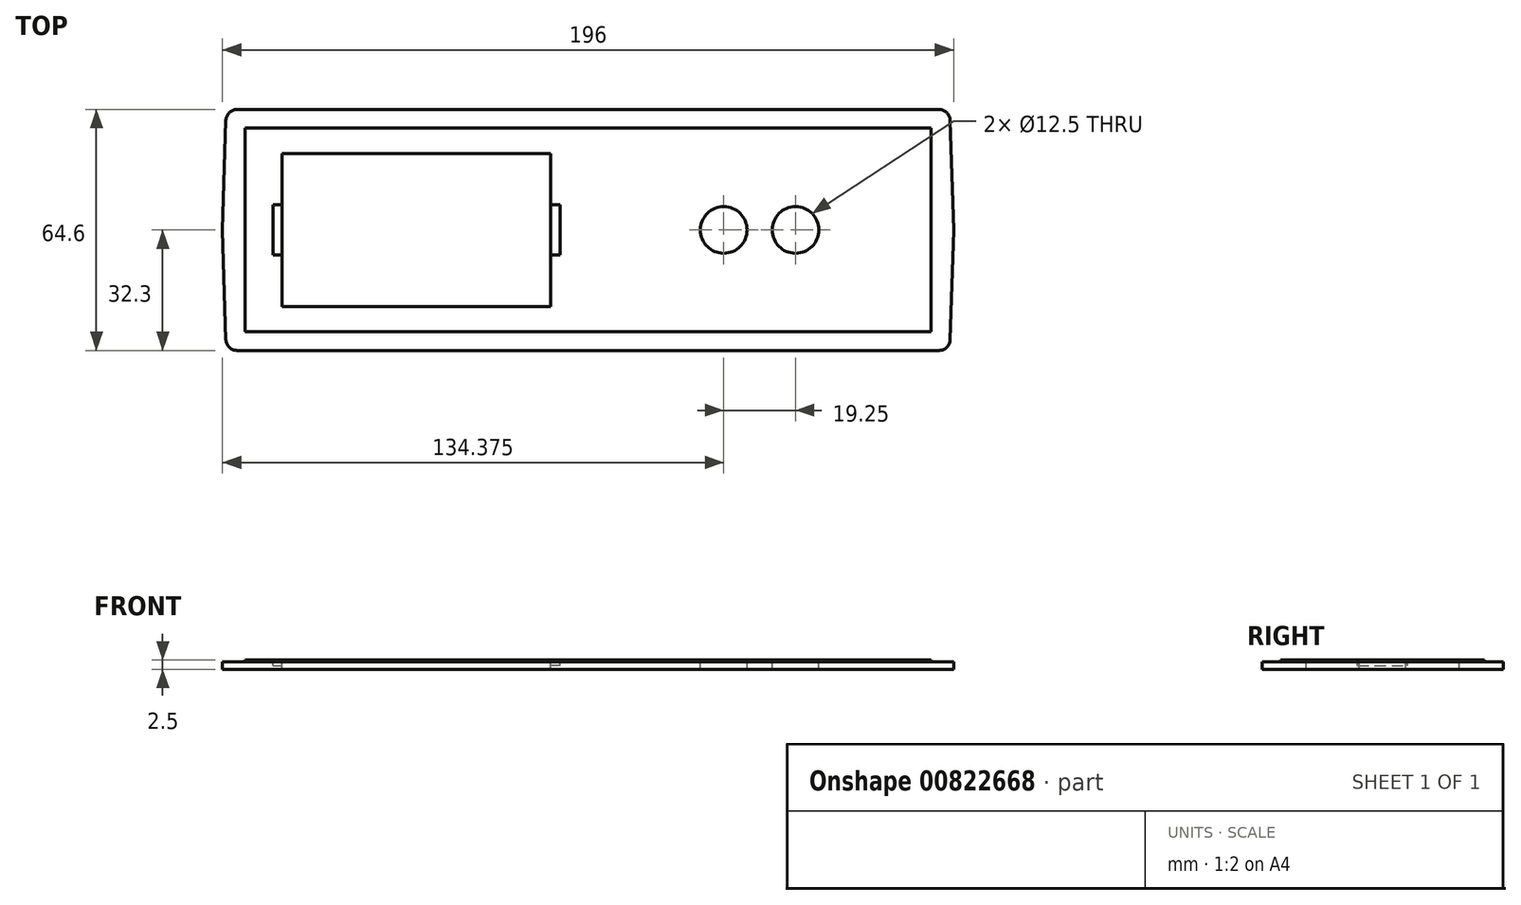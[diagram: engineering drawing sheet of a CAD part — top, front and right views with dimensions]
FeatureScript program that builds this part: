
annotation { "Feature Type Name" : "Feature", "Feature Type Description" : "" }
export const myFeature = defineFeature(function(context is Context, id is Id, definition is map)
    precondition{}
    {
        {
            var Q0;
            Q0=qCreatedBy(makeId("Top.planeOp"),FACE);
            var sketch = newSketch(context, id + "F0", { "sketchPlane" : qUnion([Q0])});
            skLineSegment(sketch, "E0.bottom", {"start": v(97, 32.3) * mm, "end": v(-97, 32.3) * mm});
            skLineSegment(sketch, "E0.top", {"start": v(97, -32.3) * mm, "end": v(-97, -32.3) * mm});
            skLineSegment(sketch, "E0.left", {"start": v(97, 32.3) * mm, "end": v(97, -32.3) * mm});
            skLineSegment(sketch, "E0.right", {"start": v(-97, 32.3) * mm, "end": v(-97, -32.3) * mm});
            skPoint(sketch, "E0.middle", {"position": v(0, 0) * mm});
            skLineSegment(sketch, "E1", {"start": v(98, 0) * mm, "end": v(97, -32.3) * mm});
            skPoint(sketch, "E1.startSnap0", {"position": v(97, 0) * mm});
            skLineSegment(sketch, "E2", {"start": v(98, 0) * mm, "end": v(97, 32.3) * mm});
            skLineSegment(sketch, "E3", {"start": v(-98, 0) * mm, "end": v(-97, 32.3) * mm});
            skLineSegment(sketch, "E4", {"start": v(-98, 0) * mm, "end": v(-97, -32.3) * mm});
            skSolve(sketch);
        }
        {
            var Q0;
            Q0=makeQuery(id+"F0.imprint","IMPRINT",FACE,{"disambiguationData":[TD([[makeQuery(id+"F0.imprint","IMPRINT",EDGE,{"derivedFrom":sQuery(id+"F0.wireOp",EDGE,"E0.bottom")}),1.0]])]});
            var Q1;
            Q1=makeQuery(id+"F0.imprint","IMPRINT",FACE,{"disambiguationData":[TD([[makeQuery(id+"F0.imprint","IMPRINT",EDGE,{"derivedFrom":sQuery(id+"F0.wireOp",EDGE,"E0.left")}),1.0]])]});
            var Q2;
            Q2=makeQuery(id+"F0.imprint","IMPRINT",FACE,{"disambiguationData":[TD([[makeQuery(id+"F0.imprint","IMPRINT",EDGE,{"derivedFrom":sQuery(id+"F0.wireOp",EDGE,"E0.right")}),-1.0]])]});
            extrude(context, id + "F1", {"entities" : qUnion([Q0, Q1, Q2]), "depth" : 2 * mm, "offsetDistance" : 25 * mm});
        }
        {
            var Q0;
            Q0=makeQuery(id+"F1.opExtrude","CAP_FACE",FACE,{"disambiguationData":[OSD([sQuery(id+"F0.wireOp",EDGE,"E0.bottom"),sQuery(id+"F0.wireOp",EDGE,"E0.top"),sQuery(id+"F0.wireOp",EDGE,"E0.left"),sQuery(id+"F0.wireOp",EDGE,"E0.right")])],"isStart":false});
            var sketch = newSketch(context, id + "F2", { "sketchPlane" : qUnion([Q0])});
            skLineSegment(sketch, "E5.bottom", {"start": v(92, 27.3) * mm, "end": v(-92, 27.3) * mm});
            skLineSegment(sketch, "E5.top", {"start": v(92, -27.3) * mm, "end": v(-92, -27.3) * mm});
            skLineSegment(sketch, "E5.left", {"start": v(92, 27.3) * mm, "end": v(92, -27.3) * mm});
            skLineSegment(sketch, "E5.right", {"start": v(-92, 27.3) * mm, "end": v(-92, -27.3) * mm});
            skPoint(sketch, "E5.middle", {"position": v(0, 0) * mm});
            skSolve(sketch);
        }
        {
            var Q0;
            Q0=makeQuery(id+"F2.imprint","IMPRINT",FACE,{"disambiguationData":[TD([[makeQuery(id+"F2.imprint","IMPRINT",EDGE,{"derivedFrom":sQuery(id+"F2.wireOp",EDGE,"E5.bottom")}),1.0]])]});
            extrude(context, id + "F3", {"entities" : qUnion([Q0]), "operationType" : NewBodyOperationType.ADD, "depth" : .5 * mm, "offsetDistance" : 25 * mm});
        }
        {
            var Q0;
            Q0=makeQuery(id+"F3.opExtrude","CAP_FACE",FACE,{"disambiguationData":[OSD([sQuery(id+"F2.wireOp",EDGE,"E5.bottom"),sQuery(id+"F2.wireOp",EDGE,"E5.top"),sQuery(id+"F2.wireOp",EDGE,"E5.left"),sQuery(id+"F2.wireOp",EDGE,"E5.right")])],"isStart":false});
            var sketch = newSketch(context, id + "F4", { "sketchPlane" : qUnion([Q0])});
            skLineSegment(sketch, "E6.bottom", {"start": v(-82, 20.5) * mm, "end": v(-10, 20.5) * mm});
            skLineSegment(sketch, "E6.top", {"start": v(-82, -20.5) * mm, "end": v(-10, -20.5) * mm});
            skLineSegment(sketch, "E6.left", {"start": v(-82, 20.5) * mm, "end": v(-82, -20.5) * mm});
            skLineSegment(sketch, "E6.right", {"start": v(-10, 20.5) * mm, "end": v(-10, -20.5) * mm});
            skLineSegment(sketch, "E7", {"start": v(-82, 20.5) * mm, "end": v(-82, 27.3) * mm, "construction": true});
            skLineSegment(sketch, "E8", {"start": v(-82, -20.5) * mm, "end": v(-82, -27.3) * mm, "construction": true});
            skLineSegment(sketch, "E9", {"start": v(-82, 20.5) * mm, "end": v(-92, 20.5) * mm, "construction": true});
            skLineSegment(sketch, "E10", {"start": v(-10, 20.5) * mm, "end": v(0, 20.5) * mm, "construction": true});
            skLineSegment(sketch, "E11.bottom", {"start": v(-84.5, 6.75) * mm, "end": v(-79.5, 6.75) * mm});
            skLineSegment(sketch, "E11.top", {"start": v(-84.5, -6.75) * mm, "end": v(-79.5, -6.75) * mm});
            skLineSegment(sketch, "E11.left", {"start": v(-84.5, 6.75) * mm, "end": v(-84.5, -6.75) * mm});
            skLineSegment(sketch, "E11.right", {"start": v(-79.5, 6.75) * mm, "end": v(-79.5, -6.75) * mm});
            skPoint(sketch, "E11.middle", {"position": v(-82, 0) * mm});
            skLineSegment(sketch, "E12.bottom", {"start": v(-7.5, 6.75) * mm, "end": v(-12.5, 6.75) * mm});
            skLineSegment(sketch, "E12.top", {"start": v(-7.5, -6.75) * mm, "end": v(-12.5, -6.75) * mm});
            skLineSegment(sketch, "E12.left", {"start": v(-7.5, 6.75) * mm, "end": v(-7.5, -6.75) * mm});
            skLineSegment(sketch, "E12.right", {"start": v(-12.5, 6.75) * mm, "end": v(-12.5, -6.75) * mm});
            skPoint(sketch, "E12.middle", {"position": v(-10, 0) * mm});
            skPoint(sketch, "E12.cornerSnap0", {"position": v(-82, 6.75) * mm});
            skCircle(sketch, "E13", {"center": v(36.37, 0) * mm, "radius": 6.25 * mm});
            skCircle(sketch, "E14", {"center": v(55.62, 0) * mm, "radius": 6.25 * mm});
            skLineSegment(sketch, "E15", {"start": v(36.37, 0) * mm, "end": v(0, 0) * mm, "construction": true});
            skLineSegment(sketch, "E16", {"start": v(55.62, 0) * mm, "end": v(92, 0) * mm, "construction": true});
            skSolve(sketch);
        }
        {
            var Q0;
            {var subQ8=sQuery(id+"F4.wireOp",EDGE,"E6.bottom");Q0=makeQuery(id+"F4.imprint","IMPRINT",FACE,{"disambiguationData":[TD([[makeQuery(id+"F4.imprint","IMPRINT",EDGE,{"derivedFrom":subQ8}),-1.0]])]});}
            var Q1;
            Q1=makeQuery(id+"F4.imprint","IMPRINT",FACE,{"disambiguationData":[TD([[makeQuery(id+"F4.imprint","IMPRINT",EDGE,{"derivedFrom":sQuery(id+"F4.wireOp",EDGE,"E13")}),1.0]])]});
            var Q2;
            Q2=makeQuery(id+"F4.imprint","IMPRINT",FACE,{"disambiguationData":[TD([[makeQuery(id+"F4.imprint","IMPRINT",EDGE,{"derivedFrom":sQuery(id+"F4.wireOp",EDGE,"E14")}),1.0]])]});
            var Q3;
            {var subQ5=sQuery(id+"F4.wireOp",EDGE,"E12.right");Q3=makeQuery(id+"F4.imprint","IMPRINT",FACE,{"disambiguationData":[TD([[makeQuery(id+"F4.imprint","IMPRINT",EDGE,{"derivedFrom":subQ5}),1.0]])]});}
            var Q4;
            {var subQ5=sQuery(id+"F4.wireOp",EDGE,"E11.right");Q4=makeQuery(id+"F4.imprint","IMPRINT",FACE,{"disambiguationData":[TD([[makeQuery(id+"F4.imprint","IMPRINT",EDGE,{"derivedFrom":subQ5}),-1.0]])]});}
            extrude(context, id + "F5", {"entities" : qUnion([Q0, Q1, Q2, Q3, Q4]), "operationType" : NewBodyOperationType.REMOVE, "oppositeDirection" : true, "depth" : 25 * mm, "offsetDistance" : 25 * mm});
        }
        {
            var Q0;
            Q0=makeQuery(id+"F1.opExtrude","SWEPT_EDGE",EDGE,{"disambiguationData":[OSD([sQuery(id+"F0.wireOp",EDGE,"E0.top"),sQuery(id+"F0.wireOp",EDGE,"E0.left")])]});
            var Q1;
            Q1=makeQuery(id+"F1.opExtrude","SWEPT_EDGE",EDGE,{"disambiguationData":[OSD([sQuery(id+"F0.wireOp",EDGE,"E0.bottom"),sQuery(id+"F0.wireOp",EDGE,"E0.left")])]});
            var Q2;
            Q2=makeQuery(id+"F1.opExtrude","SWEPT_EDGE",EDGE,{"disambiguationData":[OSD([sQuery(id+"F0.wireOp",EDGE,"E0.bottom"),sQuery(id+"F0.wireOp",EDGE,"E0.right")])]});
            var Q3;
            Q3=makeQuery(id+"F1.opExtrude","SWEPT_EDGE",EDGE,{"disambiguationData":[OSD([sQuery(id+"F0.wireOp",EDGE,"E0.top"),sQuery(id+"F0.wireOp",EDGE,"E0.right")])]});
            var Q4;
            Q4=makeQuery(id+"F1.opExtrude","SWEPT_EDGE",EDGE,{"disambiguationData":[OSD([sQuery(id+"F0.wireOp",EDGE,"E3"),sQuery(id+"F0.wireOp",EDGE,"E4")])]});
            var Q5;
            Q5=makeQuery(id+"F1.opExtrude","SWEPT_EDGE",EDGE,{"disambiguationData":[OSD([sQuery(id+"F0.wireOp",EDGE,"E1"),sQuery(id+"F0.wireOp",EDGE,"E2")])]});
            fillet(context, id + "F6", {"entities" : qUnion([Q0, Q1, Q2, Q3, Q4, Q5]), "radius" : 3 * mm, "tangentPropagation" : true, "allowEdgeOverflow" : false});
        }
        {
            var Q0;
            Q0 = qSketchRegion(id + "F4", true);
            extrude(context, id + "F7", {"entities" : qUnion([Q0]), "operationType" : NewBodyOperationType.REMOVE, "oppositeDirection" : true, "depth" : 1.5 * mm, "offsetDistance" : 25 * mm});
        }
    });
